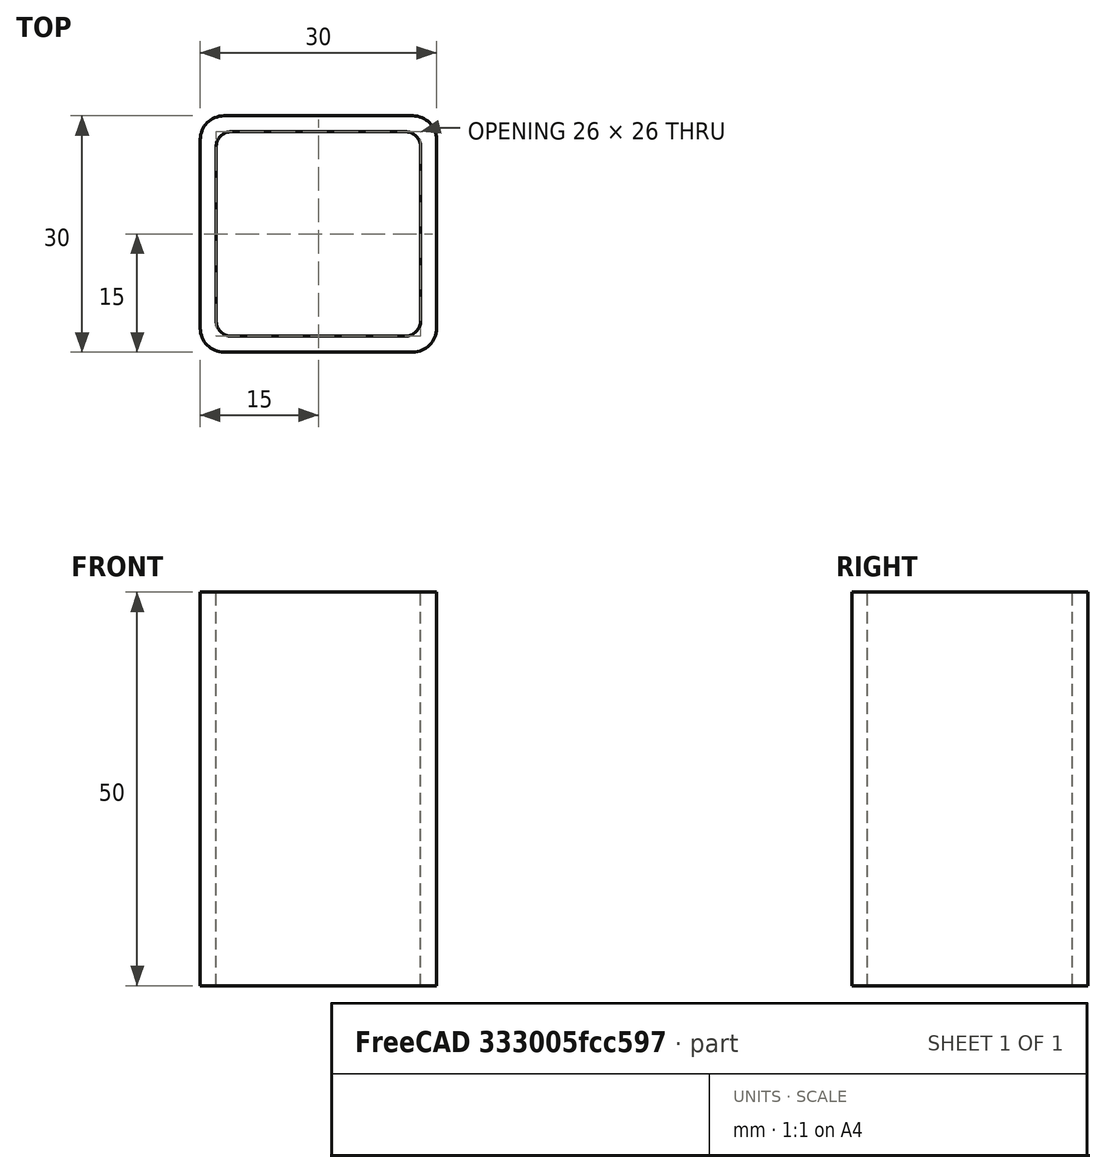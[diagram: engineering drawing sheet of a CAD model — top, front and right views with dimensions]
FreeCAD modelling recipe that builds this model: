
FCSTD DOCUMENT  (FreeCAD 0.15R4671 (Git))
Label: Square hollow section 30x30x2 EN10219 S235JRH
License: All rights reserved
LicenseURL: http://en.wikipedia.org/wiki/All_rights_reserved
objects: Sketcher::SketchObject×1, Part::Extrusion×1
note: 2 computed .brp shape members not serialized (recipe doc carries the construction recipe); baked Part::Feature solids carry a one-line shape summary decoded from their .brp

FEATURE [Sketcher::SketchObject] Sketch
  sketch-geometry (16):
    g0: LineSegment StartX=-11 StartY=13 StartZ=0 EndX=11 EndY=13 EndZ=0
    g1: LineSegment StartX=13 StartY=11 StartZ=0 EndX=13 EndY=-11 EndZ=0
    g2: LineSegment StartX=11 StartY=-13 StartZ=0 EndX=-11 EndY=-13 EndZ=0
    g3: LineSegment StartX=-13 StartY=-11 StartZ=0 EndX=-13 EndY=11 EndZ=0
    g4: LineSegment StartX=-12 StartY=15 StartZ=0 EndX=12 EndY=15 EndZ=0
    g5: LineSegment StartX=15 StartY=12 StartZ=0 EndX=15 EndY=-12 EndZ=0
    g6: LineSegment StartX=12 StartY=-15 StartZ=0 EndX=-12 EndY=-15 EndZ=0
    g7: LineSegment StartX=-15 StartY=-12 StartZ=0 EndX=-15 EndY=12 EndZ=0
    g8: ArcOfCircle CenterX=-11 CenterY=11 CenterZ=0 NormalX=0 NormalY=0 NormalZ=1 Radius=2 StartAngle=1.5708 EndAngle=3.14159
    g9: ArcOfCircle CenterX=11 CenterY=11 CenterZ=0 NormalX=0 NormalY=0 NormalZ=1 Radius=2 StartAngle=1e-12 EndAngle=1.5708
    g10: ArcOfCircle CenterX=11 CenterY=-11 CenterZ=0 NormalX=0 NormalY=0 NormalZ=1 Radius=2 StartAngle=4.71239 EndAngle=6.28319
    g11: ArcOfCircle CenterX=-11 CenterY=-11 CenterZ=0 NormalX=0 NormalY=0 NormalZ=1 Radius=2 StartAngle=3.14159 EndAngle=4.71239
    g12: ArcOfCircle CenterX=12 CenterY=12 CenterZ=0 NormalX=0 NormalY=0 NormalZ=1 Radius=3 StartAngle=0 EndAngle=1.5708
    g13: ArcOfCircle CenterX=12 CenterY=-12 CenterZ=0 NormalX=0 NormalY=0 NormalZ=1 Radius=3 StartAngle=4.71239 EndAngle=6.28319
    g14: ArcOfCircle CenterX=-12 CenterY=-12 CenterZ=0 NormalX=0 NormalY=0 NormalZ=1 Radius=3 StartAngle=3.14159 EndAngle=4.71239
    g15: ArcOfCircle CenterX=-12 CenterY=12 CenterZ=0 NormalX=0 NormalY=0 NormalZ=1 Radius=3 StartAngle=1.5708 EndAngle=3.14159
  constraints (36):
    c: Horizontal(g2)
    c: Vertical(g3)
    c: Horizontal(g6)
    c: Vertical(g7)
    c: Tangent(g3,g8) = 1.5708
    c: Tangent(g0,g8) = 1.5708
    c: Tangent(g0,g9) = 1.5708
    c: Tangent(g1,g9) = 1.5708
    c: Tangent(g1,g10) = 1.5708
    c: Tangent(g2,g10) = 1.5708
    c: Tangent(g2,g11) = 1.5708
    c: Tangent(g3,g11) = 1.5708
    c: Tangent(g4,g12) = 1.5708
    c: Tangent(g5,g12) = 1.5708
    c: Tangent(g5,g13) = 1.5708
    c: Tangent(g6,g13) = 1.5708
    c: Tangent(g6,g14) = 1.5708
    c: Tangent(g7,g14) = 1.5708
    c: Tangent(g7,g15) = 1.5708
    c: Tangent(g4,g15) = 1.5708
    c: Equal(g9,g8)
    c: Equal(g9,g11)
    c: Equal(g9,g10)
    c: Equal(g12,g15)
    c: Equal(g12,g14)
    c: Equal(g12,g13)
    c: Symmetric(g4,g6,g-1)
    c: Symmetric(g7,g5,g-2)
    c: DistanceY(g4,g6) = -30
    c: DistanceX(g7,g5) = 30
    c: Symmetric(g3,g1,g-2)
    c: Symmetric(g0,g2,g-1)
    c: DistanceY(g0,g4) = 2
    c: DistanceX(g5,g1) = -2
    c: Radius(g9) = 2
    c: Radius(g12) = 3
FEATURE [Part::Extrusion] Extrude  label="Square hollow section 30x30x2 EN10219 S235JRH"
  Base = -> Sketch
  Dir = (0,0,50)
  Solid = true
